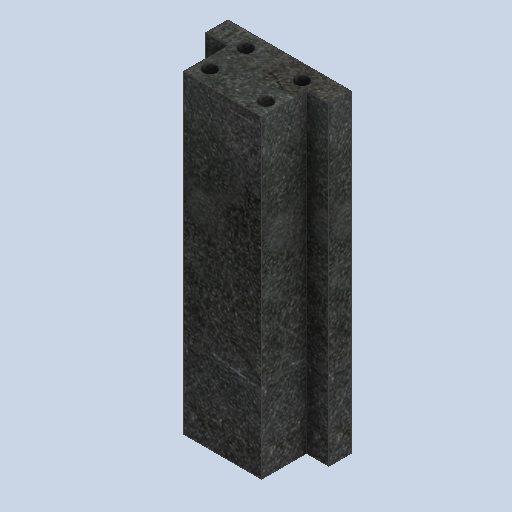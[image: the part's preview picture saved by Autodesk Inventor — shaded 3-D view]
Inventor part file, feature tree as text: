
AUTODESK INVENTOR PART (.ipt)
format: ipt  version: 2023.2 (Build 272271000, 271)  size: 314,368 bytes
history: native  units: mm
features: sketch x4, extrude x3, hole x1
ambient origin geometry x8: Origin, YZ Plane, XZ Plane, XY Plane, X Axis, Y Axis, Z Axis, Center Point
bodies: Solid1 (feature_tree)
feature tree (8):
  extrude  "Extrusion1"  Depth=55.0mm
  extrude  "Extrusion3"  Depth=10.0mm
  extrude  "Extrusion4"  Depth=6.0mm
  hole  "Hole1"  [1 undecoded]
  sketch  "Sketch1"  dims[d2=35.0mm d8=55.0mm]
  sketch  "Sketch4"  dims[d9=10.0mm d10=10.0mm]
  sketch  "Sketch5"  dims[d11=6.0mm d12=6.0mm]
  sketch  "Sketch6"  dims[d13=6.0mm d14=6.0mm d17=7.0mm d18=16.0mm d19=30.0mm d20=0.0mm d23=70.0mm d24=0.0mm d25=8.0mm d26=8.0mm d27=8.0mm d28=10.5mm d29=10.5mm d30=8.0mm d31=15.0mm d32=40.0mm d33=0.0mm d35=6.0mm d38=6.0mm d39=6.0mm d42=45.0mm d43=27.5mm d44=12.5mm d46=6.0mm d47=6.0mm d48=4.0mm d49=2.0mm d50=90.0deg d51=15.0mm d52=20.594885mm d53=6.0mm d54=6.0mm d55=6.0mm d56=45.0mm d57=45.0mm d21=0.5mm d22=0.872665mm]
note: 1 required parameter value undecoded (feature->parameter linkage not recoverable at this tier; creation-order binding heuristic only, values carry confidence <= 0.55)
